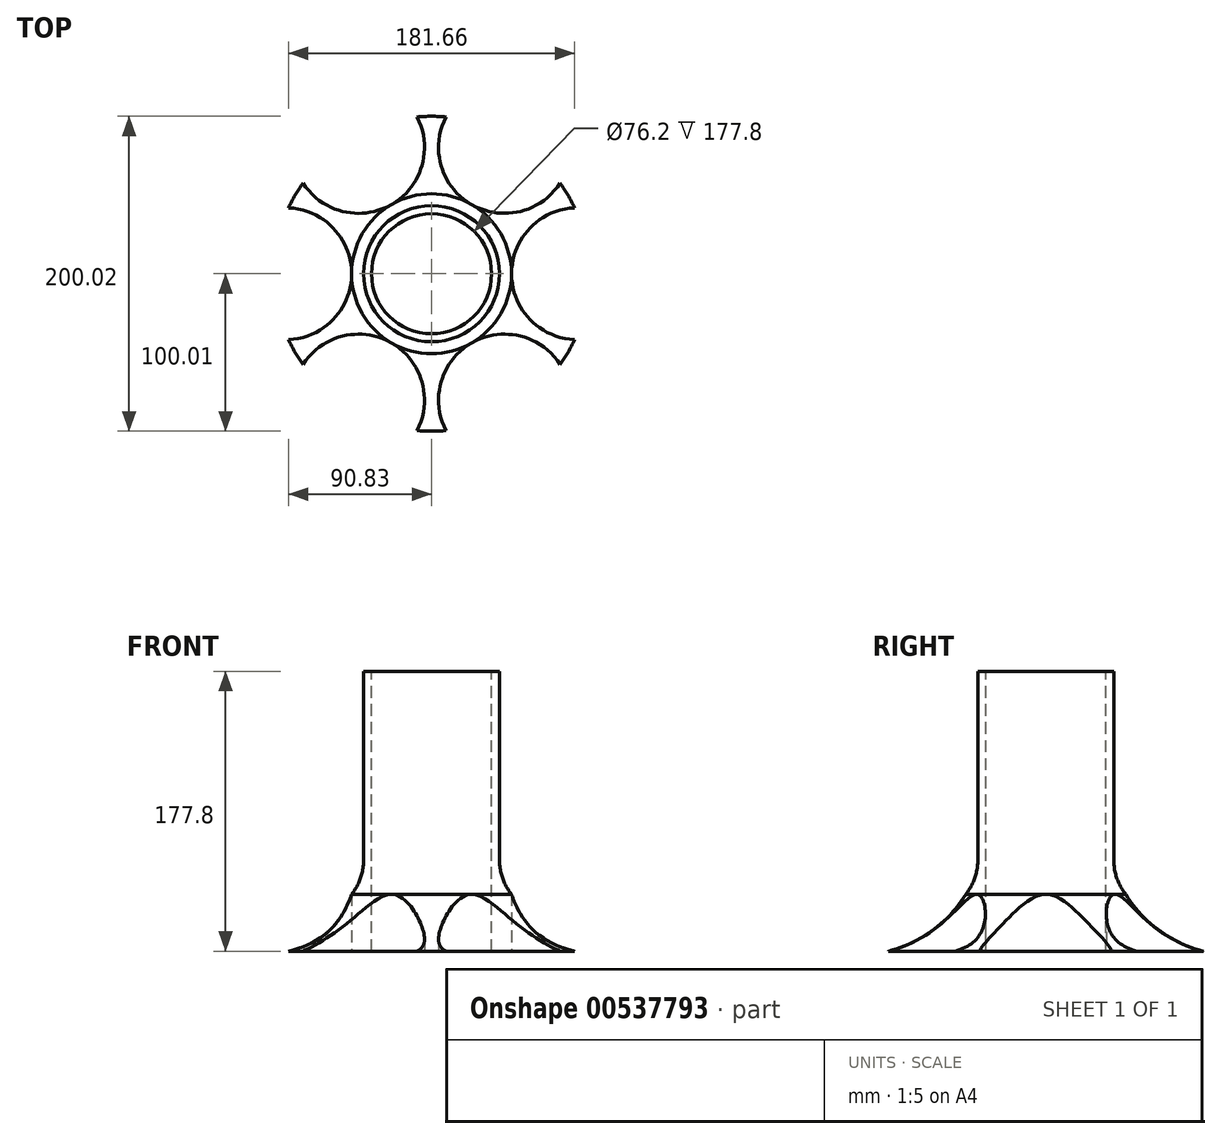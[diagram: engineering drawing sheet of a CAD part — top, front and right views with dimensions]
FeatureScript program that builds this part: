
annotation { "Feature Type Name" : "Feature", "Feature Type Description" : "" }
export const myFeature = defineFeature(function(context is Context, id is Id, definition is map)
    precondition{}
    {
        {
            var Q0;
            Q0=qCreatedBy(makeId("Top.planeOp"),FACE);
            var sketch = newSketch(context, id + "F0", { "sketchPlane" : qUnion([Q0])});
            skCircle(sketch, "E0", {"center": v(0, 0) * mm, "radius": 50.8 * mm});
            skSolve(sketch);
        }
        {
            var Q0;
            Q0=qCreatedBy(makeId("Top.planeOp"),FACE);
            var sketch = newSketch(context, id + "F1", { "sketchPlane" : qUnion([Q0])});
            skCircle(sketch, "E1", {"center": v(-92.7, 0) * mm, "radius": 41.9 * mm});
            skCircle(sketch, "E2.1.0", {"center": v(-46.36, -80.29) * mm, "radius": 41.9 * mm});
            skCircle(sketch, "E2.2.0", {"center": v(46.35, -80.29) * mm, "radius": 41.9 * mm});
            skCircle(sketch, "E2.3.0", {"center": v(92.7, 0) * mm, "radius": 41.9 * mm});
            skCircle(sketch, "E2.4.0", {"center": v(46.36, 80.29) * mm, "radius": 41.9 * mm});
            skCircle(sketch, "E2.5.0", {"center": v(-46.36, 80.29) * mm, "radius": 41.9 * mm});
            skPoint(sketch, "E2.center", {"position": v(0, 0) * mm});
            skSolve(sketch);
        }
        {
            var Q0;
            Q0=makeQuery(id+"F0.imprint","IMPRINT",FACE,{"disambiguationData":[TD([[makeQuery(id+"F0.imprint","IMPRINT",EDGE,{"derivedFrom":sQuery(id+"F0.wireOp",EDGE,"E0")}),1.0]])]});
            extrude(context, id + "F2", {"entities" : qUnion([Q0]), "depth" : 177.8 * mm, "offsetDistance" : 25.4 * mm});
        }
        {
            var Q0;
            Q0=makeQuery(id+"F2.opExtrude","CAP_FACE",FACE,{"disambiguationData":[OSD([sQuery(id+"F0.wireOp",EDGE,"E0")])],"isStart":false});
            var sketch = newSketch(context, id + "F3", { "sketchPlane" : qUnion([Q0])});
            skCircle(sketch, "E3", {"center": v(0, 0) * mm, "radius": 38.1 * mm});
            skSolve(sketch);
        }
        {
            var Q0;
            Q0=makeQuery(id+"F3.imprint","IMPRINT",FACE,{"disambiguationData":[TD([[makeQuery(id+"F3.imprint","IMPRINT",EDGE,{"derivedFrom":sQuery(id+"F3.wireOp",EDGE,"E3")}),1.0]])]});
            extrude(context, id + "F4", {"entities" : qUnion([Q0]), "operationType" : NewBodyOperationType.REMOVE, "endBound" : BoundingType.THROUGH_ALL, "oppositeDirection" : true, "depth" : 25.4 * mm, "offsetDistance" : 25.4 * mm});
        }
        {
            var Q0;
            Q0=qCreatedBy(makeId("Front.planeOp"),FACE);
            var sketch = newSketch(context, id + "F5", { "sketchPlane" : qUnion([Q0])});
            skArc(sketch, "E4", {"start": v(49.59, 38.17) * mm, "mid": v(70.94, 13.98) * mm, "end": v(100.01, 0) * mm});
            skLineSegment(sketch, "E5", {"start": v(49.59, 38.17) * mm, "end": v(49.59, 0) * mm});
            skLineSegment(sketch, "E6", {"start": v(49.59, 0) * mm, "end": v(100.01, 0) * mm});
            skSolve(sketch);
        }
        {
            var Q0;
            Q0=makeQuery(id+"F5.imprint","IMPRINT",FACE,{"disambiguationData":[TD([[makeQuery(id+"F5.imprint","IMPRINT",EDGE,{"derivedFrom":sQuery(id+"F5.wireOp",EDGE,"E4")}),-1.0]])]});
            var Q1;
            Q1=makeQuery(id+"F2.opExtrude","SWEPT_FACE",FACE,{"disambiguationData":[OSD([sQuery(id+"F0.wireOp",EDGE,"E0")])]});
            revolve(context, id + "F6", {"operationType" : NewBodyOperationType.ADD, "entities" : qUnion([Q0]), "axis" : qUnion([Q1]), "revolveType" : RevolveType.FULL});
        }
        {
            var Q0;
            Q0 = qSketchRegion(id + "F1", true);
            extrude(context, id + "F7", {"entities" : qUnion([Q0]), "operationType" : NewBodyOperationType.REMOVE, "endBound" : BoundingType.THROUGH_ALL, "depth" : 25.4 * mm, "offsetDistance" : 25.4 * mm});
        }
        {
            var Q0;
            Q0=qCreatedBy(makeId("Front.planeOp"),FACE);
            var sketch = newSketch(context, id + "F8", { "sketchPlane" : qUnion([Q0])});
            skArc(sketch, "E7", {"start": v(-50.8, 36.13) * mm, "mid": v(-45.14, 46.38) * mm, "end": v(-43.18, 57.91) * mm});
            skLineSegment(sketch, "E8", {"start": v(-43.18, 57.91) * mm, "end": v(-43.18, 177.8) * mm});
            skLineSegment(sketch, "E9", {"start": v(-43.18, 177.8) * mm, "end": v(-50.8, 177.8) * mm});
            skLineSegment(sketch, "E10", {"start": v(-50.8, 177.8) * mm, "end": v(-50.8, 36.13) * mm});
            skSolve(sketch);
        }
        {
            var Q0;
            Q0=makeQuery(id+"F8.imprint","IMPRINT",FACE,{"disambiguationData":[TD([[makeQuery(id+"F8.imprint","IMPRINT",EDGE,{"derivedFrom":sQuery(id+"F8.wireOp",EDGE,"E7")}),1.0]])]});
            var Q1;
            Q1=makeQuery(id+"F2.opExtrude","CAP_EDGE",EDGE,{"disambiguationData":[OSD([sQuery(id+"F0.wireOp",EDGE,"E0")])],"isStart":false});
            revolve(context, id + "F9", {"operationType" : NewBodyOperationType.REMOVE, "entities" : qUnion([Q0]), "axis" : qUnion([Q1]), "revolveType" : RevolveType.FULL, "oppositeDirection" : true});
        }
    });
